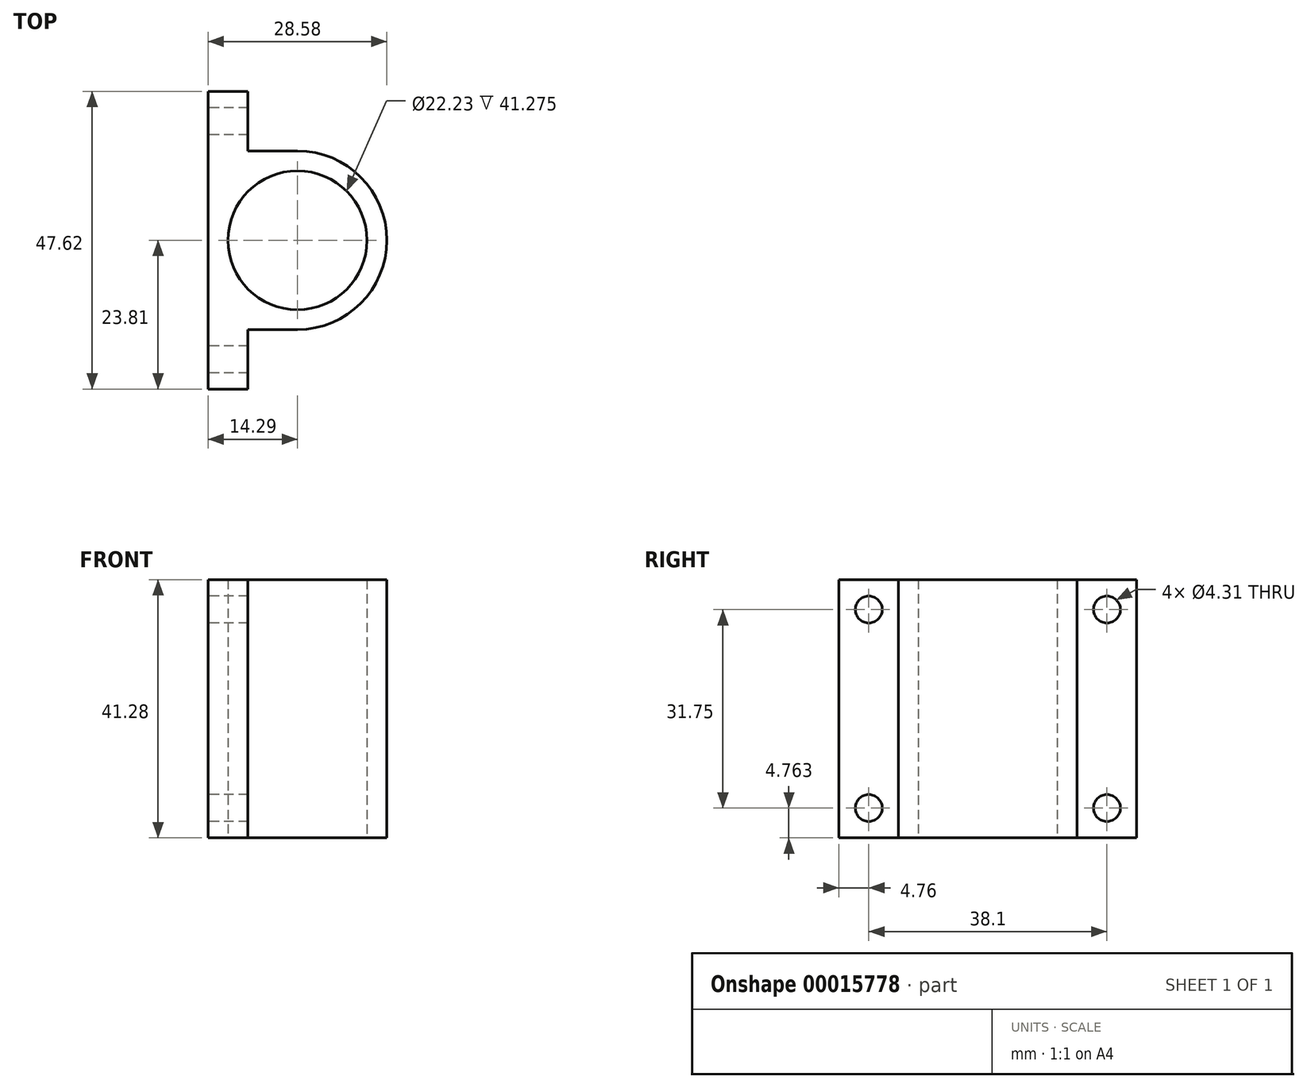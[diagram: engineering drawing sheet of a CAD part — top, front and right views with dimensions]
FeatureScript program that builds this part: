
annotation { "Feature Type Name" : "Feature", "Feature Type Description" : "" }
export const myFeature = defineFeature(function(context is Context, id is Id, definition is map)
    precondition{}
    {
        {
            var Q0;
            Q0=qCreatedBy(makeId("Top.planeOp"),FACE);
            var sketch = newSketch(context, id + "F0", { "sketchPlane" : qUnion([Q0])});
            skCircle(sketch, "E0", {"center": v(0, 0) * mm, "radius": 11.11 * mm});
            skLineSegment(sketch, "E1", {"start": v(0, 14.29) * mm, "end": v(0, -14.29) * mm});
            skArc(sketch, "E2", {"start": v(0, -14.29) * mm, "mid": v(14.29, 0) * mm, "end": v(0, 14.29) * mm});
            skLineSegment(sketch, "E3", {"start": v(0, 14.29) * mm, "end": v(-7.94, 14.29) * mm});
            skLineSegment(sketch, "E4", {"start": v(0, -14.29) * mm, "end": v(-7.94, -14.29) * mm});
            skLineSegment(sketch, "E5", {"start": v(-7.94, -14.29) * mm, "end": v(-7.94, -23.81) * mm});
            skLineSegment(sketch, "E6", {"start": v(-7.94, -23.81) * mm, "end": v(-14.29, -23.81) * mm});
            skLineSegment(sketch, "E7", {"start": v(-14.29, -23.81) * mm, "end": v(-14.29, 23.81) * mm});
            skLineSegment(sketch, "E8", {"start": v(-14.29, 23.81) * mm, "end": v(-7.94, 23.81) * mm});
            skLineSegment(sketch, "E9", {"start": v(-7.94, 23.81) * mm, "end": v(-7.94, 14.29) * mm});
            skLineSegment(sketch, "E10", {"start": v(0, 0) * mm, "end": v(-11.11, 0) * mm, "construction": true});
            skLineSegment(sketch, "E11", {"start": v(-11.11, 0) * mm, "end": v(-14.29, 0) * mm, "construction": true});
            skLineSegment(sketch, "E12", {"start": v(-7.94, -14.29) * mm, "end": v(-11.11, -14.29) * mm, "construction": true});
            skLineSegment(sketch, "E13", {"start": v(-11.11, -14.29) * mm, "end": v(-14.29, -14.29) * mm, "construction": true});
            skSolve(sketch);
        }
        {
            var Q0;
            Q0 = qSketchRegion(id + "F0", true);
            extrude(context, id + "F1", {"entities" : qUnion([Q0]), "depth" : 41.27 * mm});
        }
        {
            var Q0;
            Q0=makeQuery(id+"F1.opExtrude","SWEPT_FACE",FACE,{"disambiguationData":[OSD([sQuery(id+"F0.wireOp",EDGE,"E7")])]});
            var sketch = newSketch(context, id + "F2", { "sketchPlane" : qUnion([Q0])});
            skLineSegment(sketch, "E14", {"start": v(0, 41.28) * mm, "end": v(0, 0) * mm, "construction": true});
            skLineSegment(sketch, "E15", {"start": v(19.05, 41.28) * mm, "end": v(19.05, 36.51) * mm, "construction": true});
            skLineSegment(sketch, "E16", {"start": v(19.05, 36.51) * mm, "end": v(23.81, 36.51) * mm, "construction": true});
            skLineSegment(sketch, "E17.bottom", {"start": v(19.05, 36.51) * mm, "end": v(-19.05, 36.51) * mm, "construction": true});
            skLineSegment(sketch, "E17.top", {"start": v(19.05, 4.76) * mm, "end": v(-19.05, 4.76) * mm, "construction": true});
            skLineSegment(sketch, "E17.left", {"start": v(19.05, 36.51) * mm, "end": v(19.05, 4.76) * mm, "construction": true});
            skLineSegment(sketch, "E17.right", {"start": v(-19.05, 36.51) * mm, "end": v(-19.05, 4.76) * mm, "construction": true});
            skPoint(sketch, "E17.middle", {"position": v(0, 20.64) * mm});
            skCircle(sketch, "E18", {"center": v(19.05, 36.51) * mm, "radius": 2.15 * mm});
            skCircle(sketch, "E19", {"center": v(19.05, 4.76) * mm, "radius": 2.15 * mm});
            skCircle(sketch, "E20", {"center": v(-19.05, 36.51) * mm, "radius": 2.15 * mm});
            skCircle(sketch, "E21", {"center": v(-19.05, 4.76) * mm, "radius": 2.15 * mm});
            skSolve(sketch);
        }
        {
            var Q0;
            Q0 = qSketchRegion(id + "F2", true);
            var Q1;
            Q1=makeQuery(id+"F1.opExtrude","SWEPT_FACE",FACE,{"disambiguationData":[OSD([sQuery(id+"F0.wireOp",EDGE,"E9")])]});
            extrude(context, id + "F3", {"entities" : qUnion([Q0]), "operationType" : NewBodyOperationType.REMOVE, "endBound" : BoundingType.UP_TO_SURFACE, "oppositeDirection" : true, "endBoundEntityFace" : qUnion([Q1]), "depth" : 25.4 * mm});
        }
    });
